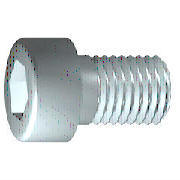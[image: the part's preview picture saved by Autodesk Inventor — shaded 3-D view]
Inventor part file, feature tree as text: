
AUTODESK INVENTOR PART (.ipt)
format: ipt  version: 2013 (Build 170138000, 138)  size: 186,368 bytes
history: native  units: mm (DEFAULTED — no unit token found)
features: sketch x2, extrude x1, plane x1, fillet x1
ambient origin geometry x7: Origin, YZ Plane, XY Plane, X Axis, Y Axis, Z Axis, Center Point
bodies: Solid1 (feature_tree), Body (feature_tree)
feature tree (5):
  extrude  "Slot"  Depth=0.306825mm
  plane  "Work Plane1"
  fillet  "Fillet2"  Radius=3.0mm
  sketch  "Sketch1"  dims[d1=19.08655mm d2=0.306825mm d3=3.0mm]
  sketch  "Sketch2"  dims[d4=1.5mm d5=60.0deg d6=3.0mm d7=3.0mm d8=2.886751mm d9=5.5mm d10=90.0deg d11=10.0mm d12=0.0mm d13=19.08655mm d14=0.0mm d15=0.306725mm d16=0.306725mm d17=0.3mm d19=0.0mm d26=20.0mm d27=45.0deg d28=0.0mm d29=0.0mm d30=0.1mm]
